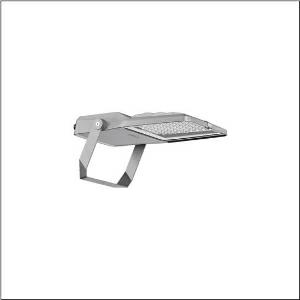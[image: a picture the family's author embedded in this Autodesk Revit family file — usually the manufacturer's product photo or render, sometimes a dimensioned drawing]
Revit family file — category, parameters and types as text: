
# Revit family: floodlight_fl_21_iq_mini___pl52_5xa7772b5d1a_4874
name_source: partatom
category: Lighting Fixtures
units: mm (PartAtom-declared; Revit-internal decimal feet)

## family parameters
Cut with Voids When Loaded = No
Host = Face
Light Source = No
Part Type = Normal
Room Calculation Point = No
Round Connector Dimension = Use Diameter
Shared = No

## types (1)
- --- (1 x LED, 5820 lm, 45.5 W, 4000K)
    Apparent Load = 46 VA
    CIE Flux Codes = 26 60 98 100 100
    Color Rendering = 80
    Color Temperature = 4000K
    Default Elevation = 1800 mm
    Description = Floodlight FL 21 iQ mini, floodlight, primary light control with lens, of PMMA, primary optical cover: protective disc, of toughened safety glass, transparent, light distribution: PL52, light emission: direct distribution, installation type: surface-mounted, LED, High Power LED, rated luminous flux: 5.820lm, luminous efficacy: 128lm/W, light colour: 840, colour temperature: 4000K, control gear: iQ Street-Remote/DALI, control: Street-Remote, Auto-Match, Temp-Guard, Night-Set, Smart-Wire, Desk-Remote (wireless, voltage-free reading and setting of iQ features in the workshop via application-optimized NFC function/RFID function), optimised constant luminous flux control (CLO 2.0), with terminal, 6-pole, mains connection: 220..240V, AC, 50/60Hz, start of lifetime: 46W, end of service life: 48W, reduction: 22W, luminaire housing, of diecast aluminium, powder-coated, Siteco® metallic grey (DB 702S), corrosivity category C5 mid according to DIN EN ISO 12944, suitable for swimming pools, chlorine-resistant, sealing non-destructively replaceable, mounting bracket, of steel, galvanised, powder-coated, Siteco® metallic grey (DB 702S), protection rating (complete): IP66, insulation class (complete): insulation class II (safety insulation), certification: CE, ENEC, VDE, protection symbol: D, impact resistance: IK08, permissible operating ambient temperature: -40..+40°C, permissible operating ambient temperature for outdoor applications: -40..+50°C, standard: DIN EN 12944, LABS conformity tested according to VDMA 24364:2018-05, packaging unit: 1 piece

Light Distribution: PL52
    Height = 70 mm
    Lamp = 1 x LED
    Lamp Light Flux = 5820 lm
    Lamp Power = 45.5 W
    Lamp count = 1
    Length = 485 mm
    Luminous efficacy = 128 lm/W
    Manufacturer = Siteco
    ModVariant = No
    Model = 5XA7772B5D1A
    Number of Poles = 1
    OnlyDefault = Yes
    Power Factor = 1
    Product Name = Floodlight FL 21 iQ mini | PL52
    Product group = floodlight | pylon annexe
    ProductGroupID = 6200
    Protection Class = Protection class II
    Protection Degree = IP 66
    RLX_Detail_Level = 1
    RLX_Emergency_Light_Flux = 0 lm
    RLX_Emergency_Type = 0
    RLX_Emergency_Type_DB = No
    RlxData = <blob elided: 96397 chars, md5=0ec018d7>
    Socket = socket
    Standby Power = 0 W
    System Light Flux = 5820 lm
    System Power = 46 W
    Type Comments = factory setting: luminous flux: 100 % | dim-lin: 254 | 463 mA
    Type Image = l_1006845.jpg
    URL = http://relux.com
    VarID = @adj_164664
    Voltage = 0 V
    Weight = 0.00 kg
    Width = 337 mm

## geometry (parser evidence)
native form markers: Blend x4, Sweep x12
no freeform markers — native parametric forms only
